# Revit family: Drinking_Fountain-Bi_Level-Murdock-Classic-MC76D_Series
name_source: partatom
category: Plumbing Fixtures
units: mm (PartAtom-declared; Revit-internal decimal feet)

## family parameters
Cut with Voids When Loaded = No
Host = Face
OmniClass Number = 23.65.70.14.11
OmniClass Title = Drinking Fountains/Coolers
Part Type = Normal
Room Calculation Point = No
Round Connector Dimension = Use Diameter
Shared = Yes

## types (4) — shared parameters
ADA Compliant = Yes
Assembly Code = D2010810
CW Connection = Yes
CWFU = 1.5
Chrome Plated Bubbler = Yes
Chrome plated cast brass bowl = No
Compliance Certifications = ASTM standards B61 and B62. Unit shall conform to ANSI/NSF 61-9, and Public Law 111-380.
Description = Two Bowls on Arms Classic Style Drinking Fountain
Drain Hose Connection Diameter = 7/8"
HW Connection = No
Height = 35 1/4"
Inlet Connection Diameter = 1/4"
Installation Instruction Link = https://www.murdockmfg.com
Installation Type = Pedestal
Manufacturer = Murdock
Operating Pressure = 30 to 100 psi
Outlet Connection Diameter = 2"
Powder-coated cast brass bowl = Yes
Product Documentation Link = https://www.murdockmfg.com
Product Page URL = https://www.murdockmfg.com
Tempered Water Connection = No
URL = http://www.murdockmfg.com
Vent Connection = No
WFU = 2
Waste Connection = Yes
Width = 45 1/8"
zero-valued in all types: HWFU

## per-type parameters (varying)
| type | Black - Pedestal color black | Bowl Finish | Brown- Pedestal color Brown | Default Elevation | FRU2 - Underground Freeze-Resistant Valve for Two Bowls | FRU3 - Underground Freeze-Resistant Valve for Three Bowls | Green - Pedestal color green | PF - Pet Fountain with pushbutton valve | Pedestal Finish |
| M-C76D | Yes | Cast Brass-Murdock-Polished | No | 0" | Yes | No | No | No | Cast Iron-Murdock-Black |
| M-C76D-Green | No | Cast Brass-Murdock-Chrome Plated | No | 34" | Yes | No | Yes | No | Cast Iron-Murdock-Green |
| M-C76D-PF | Yes | Cast Brass-Murdock-Polished | No | 0" | No | Yes | No | Yes | Cast Iron-Murdock-Black |
| M-C76D-Brown | No | Cast Brass-Murdock-Polished | Yes | 0" | Yes | No | No | No | Cast Iron-Murdock-Brown |

note: column(s) folded — value = type name in every type: Model

## geometry (parser evidence)
native form markers: Sweep x2
no freeform markers — native parametric forms only
